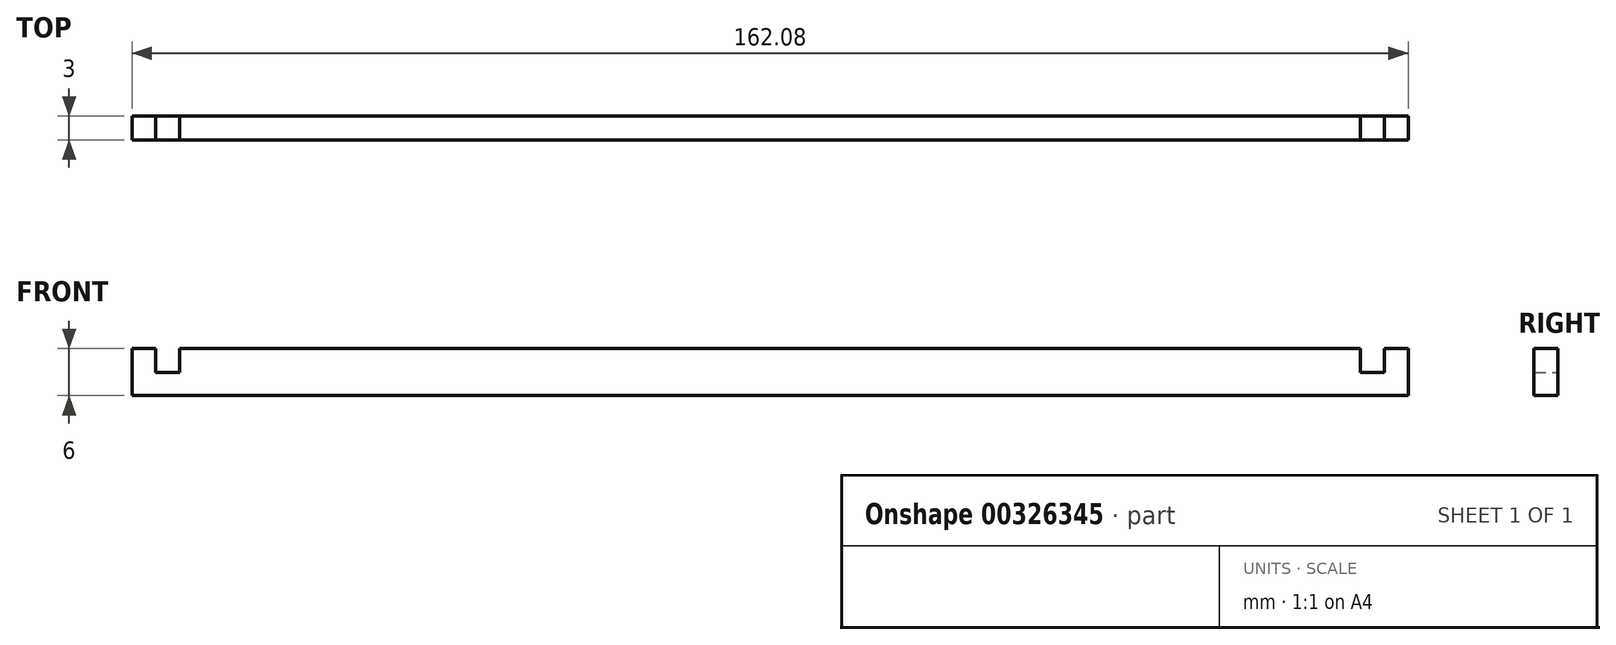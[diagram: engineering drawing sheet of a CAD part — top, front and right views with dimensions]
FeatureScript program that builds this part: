
annotation { "Feature Type Name" : "Feature", "Feature Type Description" : "" }
export const myFeature = defineFeature(function(context is Context, id is Id, definition is map)
    precondition{}
    {
        {
            var Q0;
            Q0=qCreatedBy(makeId("Front.planeOp"),FACE);
            var sketch = newSketch(context, id + "F0", { "sketchPlane" : qUnion([Q0])});
            skLineSegment(sketch, "E0", {"start": v(-81.04, 0) * mm, "end": v(-81.04, 6) * mm});
            skLineSegment(sketch, "E1", {"start": v(-81.04, 6) * mm, "end": v(-78.04, 6) * mm});
            skLineSegment(sketch, "E2", {"start": v(81.04, 6) * mm, "end": v(81.04, 0) * mm});
            skPoint(sketch, "E3", {"position": v(-78.04, 2.98) * mm});
            skPoint(sketch, "E4", {"position": v(-75, 2.98) * mm});
            skPoint(sketch, "E5", {"position": v(78.04, 2.98) * mm});
            skPoint(sketch, "E6", {"position": v(75, 2.98) * mm});
            skLineSegment(sketch, "E7", {"start": v(-75, 2.98) * mm, "end": v(-78.04, 2.98) * mm});
            skLineSegment(sketch, "E8", {"start": v(78.04, 2.98) * mm, "end": v(75, 2.98) * mm});
            skLineSegment(sketch, "E9", {"start": v(-81.04, 0) * mm, "end": v(81.04, 0) * mm});
            skLineSegment(sketch, "E10", {"start": v(78.04, 2.98) * mm, "end": v(78.04, 6) * mm});
            skLineSegment(sketch, "E11", {"start": v(75, 2.98) * mm, "end": v(75, 6) * mm});
            skLineSegment(sketch, "E12", {"start": v(-78.04, 2.98) * mm, "end": v(-78.04, 6) * mm});
            skLineSegment(sketch, "E13", {"start": v(-75, 2.98) * mm, "end": v(-75, 6) * mm});
            skLineSegment(sketch, "E14.trimOffspring", {"start": v(-75, 6) * mm, "end": v(75, 6) * mm});
            skLineSegment(sketch, "E15.trimOffspring", {"start": v(78.04, 6) * mm, "end": v(81.04, 6) * mm});
            skSolve(sketch);
        }
        {
            var Q0;
            Q0=makeQuery(id+"F0.imprint","IMPRINT",FACE,{"disambiguationData":[TD([[makeQuery(id+"F0.imprint","IMPRINT",EDGE,{"derivedFrom":sQuery(id+"F0.wireOp",EDGE,"daeca98d-3240-409c-9885-89564d3c6af8")}),-1.0]])]});
            var Q1;
            Q1=makeQuery(id+"F0.imprint","IMPRINT",FACE,{"disambiguationData":[TD([[makeQuery(id+"F0.imprint","IMPRINT",EDGE,{"derivedFrom":sQuery(id+"F0.wireOp",EDGE,"E0")}),-1.0]])]});
            extrude(context, id + "F1", {"entities" : qUnion([Q0, Q1]), "depth" : 3 * mm});
        }
    });
